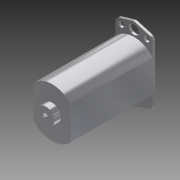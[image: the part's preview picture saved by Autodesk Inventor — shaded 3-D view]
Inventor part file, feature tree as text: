
AUTODESK INVENTOR PART (.ipt)
format: ipt  version: 2015 SP1 (Build 190203100, 203)  size: 119,808 bytes
history: native  units: in
note: dims shown in document units (in); Inventor stores cm internally (conversion verified against a paired STEP export)
features: other x2, imported_body x2, fillet x1
ambient origin geometry x8: Origin, YZ Plane, XZ Plane, XY Plane, X Axis, Y Axis, Z Axis, Center Point
bodies: Body1 (feature_tree), Body2 (feature_tree)
feature tree (5):
  fillet  "Fillet1"  [1 undecoded]
  other  "AM-2235 motor.ipt1"
  other  "Boss-Extrude4"
  imported_body  "Base1"
  imported_body  "Base2"
note: 1 required parameter value undecoded (feature->parameter linkage not recoverable at this tier; creation-order binding heuristic only, values carry confidence <= 0.55)
